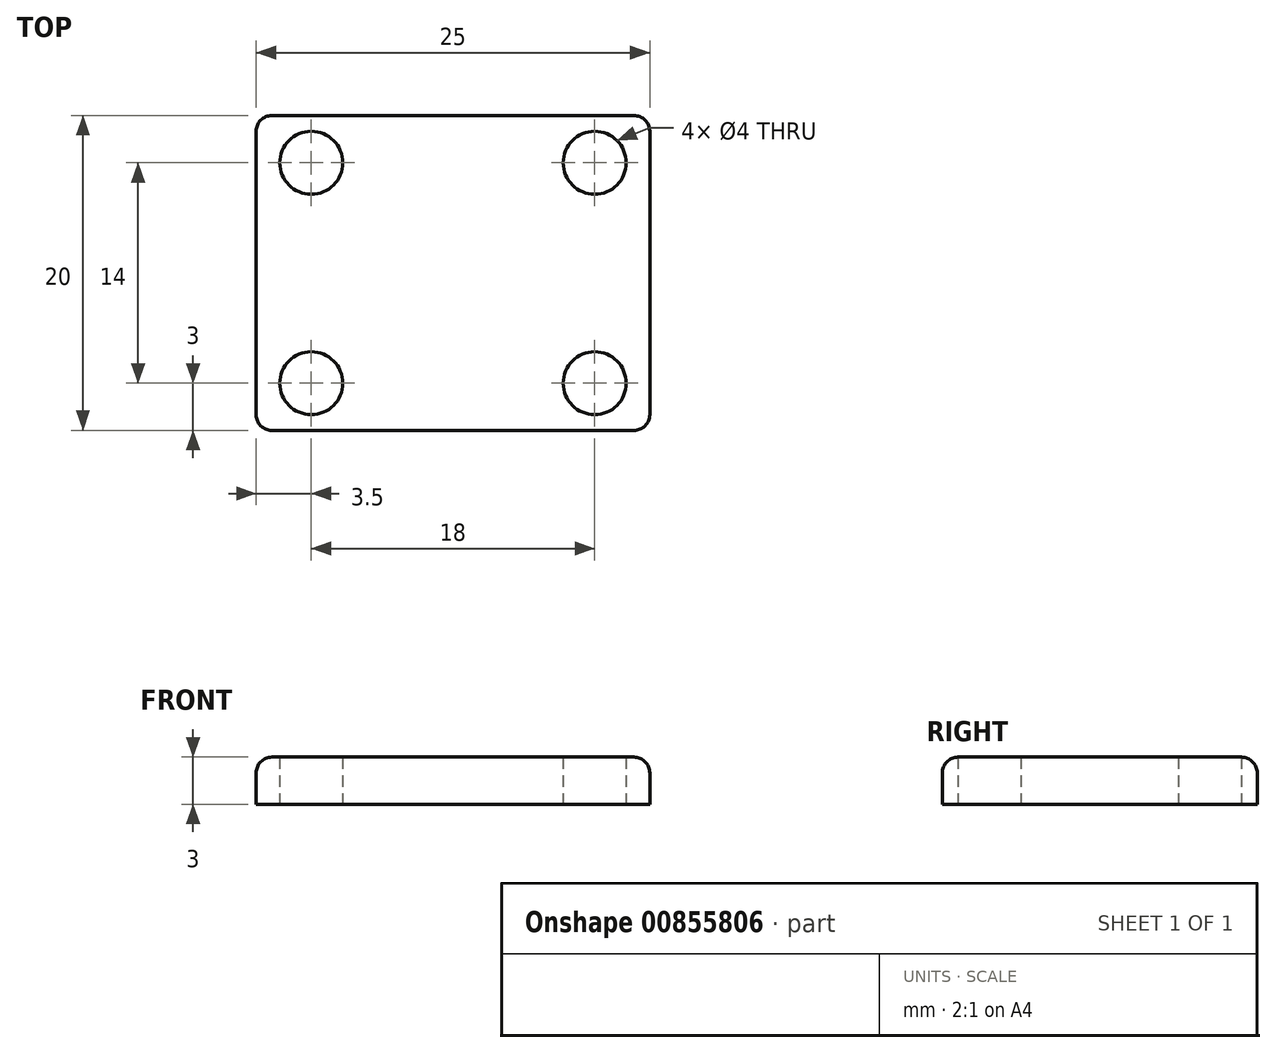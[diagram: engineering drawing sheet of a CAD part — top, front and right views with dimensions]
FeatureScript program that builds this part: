
annotation { "Feature Type Name" : "Feature", "Feature Type Description" : "" }
export const myFeature = defineFeature(function(context is Context, id is Id, definition is map)
    precondition{}
    {
        {
            var Q0;
            Q0=qCreatedBy(makeId("Top.planeOp"),FACE);
            var sketch = newSketch(context, id + "F0", { "sketchPlane" : qUnion([Q0])});
            skLineSegment(sketch, "E0.bottom", {"start": v(12.5, 5.13) * mm, "end": v(-12.5, 5.13) * mm});
            skLineSegment(sketch, "E0.top", {"start": v(12.5, -5.12) * mm, "end": v(-12.5, -5.12) * mm});
            skLineSegment(sketch, "E0.left", {"start": v(12.5, 5.13) * mm, "end": v(12.5, -5.12) * mm});
            skLineSegment(sketch, "E0.right", {"start": v(-12.5, 5.13) * mm, "end": v(-12.5, -5.12) * mm});
            skPoint(sketch, "E0.middle", {"position": v(0, 0) * mm});
            skLineSegment(sketch, "E1.bottom", {"start": v(12.5, 10) * mm, "end": v(-12.5, 10) * mm});
            skLineSegment(sketch, "E1.top", {"start": v(12.5, -10) * mm, "end": v(-12.5, -10) * mm});
            skLineSegment(sketch, "E1.left", {"start": v(12.5, 10) * mm, "end": v(12.5, -10) * mm});
            skLineSegment(sketch, "E1.right", {"start": v(-12.5, 10) * mm, "end": v(-12.5, -10) * mm});
            skSolve(sketch);
        }
        {
            var Q0;
            {var subQ0=sQuery(id+"F0.wireOp",EDGE,"E0.bottom");var subQ1=makeQuery(id+"F0.imprint","IMPRINT",EDGE,{"derivedFrom":subQ0});var subQ2=sQuery(id+"F0.wireOp",EDGE,"E0.top");var subQ3=makeQuery(id+"F0.imprint","IMPRINT",EDGE,{"derivedFrom":subQ2});Q0=qUnion([makeQuery(id+"F0.imprint","IMPRINT",FACE,{"disambiguationData":[TD([[subQ1,-1.0]])]}),makeQuery(id+"F0.imprint","IMPRINT",FACE,{"disambiguationData":[TD([[subQ3,1.0]])]}),makeQuery(id+"F0.imprint","IMPRINT",FACE,{"disambiguationData":[TD([[subQ1,1.0]])]})]);}
            extrude(context, id + "F1", {"entities" : qUnion([Q0]), "depth" : 3 * mm, "offsetDistance" : 25 * mm});
        }
        {
            var Q0;
            Q0=makeQuery(id+"F1.opExtrude","CAP_EDGE",EDGE,{"disambiguationData":[OSD([sQuery(id+"F0.wireOp",EDGE,"E1.top")])],"isStart":false});
            var Q1;
            Q1=makeQuery(id+"F1.opExtrude","CAP_EDGE",EDGE,{"disambiguationData":[OSD([sQuery(id+"F0.wireOp",EDGE,"E0.left"),sQuery(id+"F0.wireOp",EDGE,"E1.left")])],"isStart":false});
            var Q2;
            Q2=makeQuery(id+"F1.opExtrude","CAP_EDGE",EDGE,{"disambiguationData":[OSD([sQuery(id+"F0.wireOp",EDGE,"E1.bottom")])],"isStart":false});
            var Q3;
            Q3=makeQuery(id+"F1.opExtrude","CAP_EDGE",EDGE,{"disambiguationData":[OSD([sQuery(id+"F0.wireOp",EDGE,"E0.right"),sQuery(id+"F0.wireOp",EDGE,"E1.right")])],"isStart":false});
            var Q4;
            Q4=makeQuery(id+"F1.opExtrude","SWEPT_EDGE",EDGE,{"disambiguationData":[OSD([sQuery(id+"F0.wireOp",EDGE,"E1.top"),sQuery(id+"F0.wireOp",EDGE,"E1.left")])]});
            var Q5;
            Q5=makeQuery(id+"F1.opExtrude","SWEPT_EDGE",EDGE,{"disambiguationData":[OSD([sQuery(id+"F0.wireOp",EDGE,"E1.top"),sQuery(id+"F0.wireOp",EDGE,"E1.right")])]});
            var Q6;
            Q6=makeQuery(id+"F1.opExtrude","SWEPT_EDGE",EDGE,{"disambiguationData":[OSD([sQuery(id+"F0.wireOp",EDGE,"E1.bottom"),sQuery(id+"F0.wireOp",EDGE,"E1.right")])]});
            var Q7;
            Q7=makeQuery(id+"F1.opExtrude","SWEPT_EDGE",EDGE,{"disambiguationData":[OSD([sQuery(id+"F0.wireOp",EDGE,"E1.bottom"),sQuery(id+"F0.wireOp",EDGE,"E1.left")])]});
            fillet(context, id + "F2", {"entities" : qUnion([Q0, Q1, Q2, Q3, Q4, Q5, Q6, Q7]), "radius" : 1 * mm, "tangentPropagation" : true, "allowEdgeOverflow" : false});
        }
        {
            var Q0;
            {var subQ0=sQuery(id+"F0.wireOp",EDGE,"E0.top");Q0=makeQuery(id+"F0.imprint","IMPRINT",FACE,{"disambiguationData":[TD([[makeQuery(id+"F0.imprint","IMPRINT",EDGE,{"derivedFrom":subQ0}),1.0]])]});}
            var sketch = newSketch(context, id + "F3", { "sketchPlane" : qUnion([Q0])});
            skLineSegment(sketch, "E2", {"start": v(0, 0) * mm, "end": v(-9, 0) * mm});
            skLineSegment(sketch, "E3", {"start": v(-9, 0) * mm, "end": v(-9, -7) * mm});
            skCircle(sketch, "E4", {"center": v(-9, -7) * mm, "radius": 2 * mm});
            skCircle(sketch, "E5.MirrorC", {"center": v(9, -7) * mm, "radius": 2 * mm});
            skCircle(sketch, "E6.MirrorC", {"center": v(9, 7) * mm, "radius": 2 * mm});
            skCircle(sketch, "E7.MirrorC", {"center": v(-9, 7) * mm, "radius": 2 * mm});
            skSolve(sketch);
        }
        {
            var Q0;
            Q0 = qSketchRegion(id + "F3", true);
            extrude(context, id + "F4", {"entities" : qUnion([Q0]), "operationType" : NewBodyOperationType.REMOVE, "depth" : 68 * mm, "offsetDistance" : 25 * mm});
        }
    });
